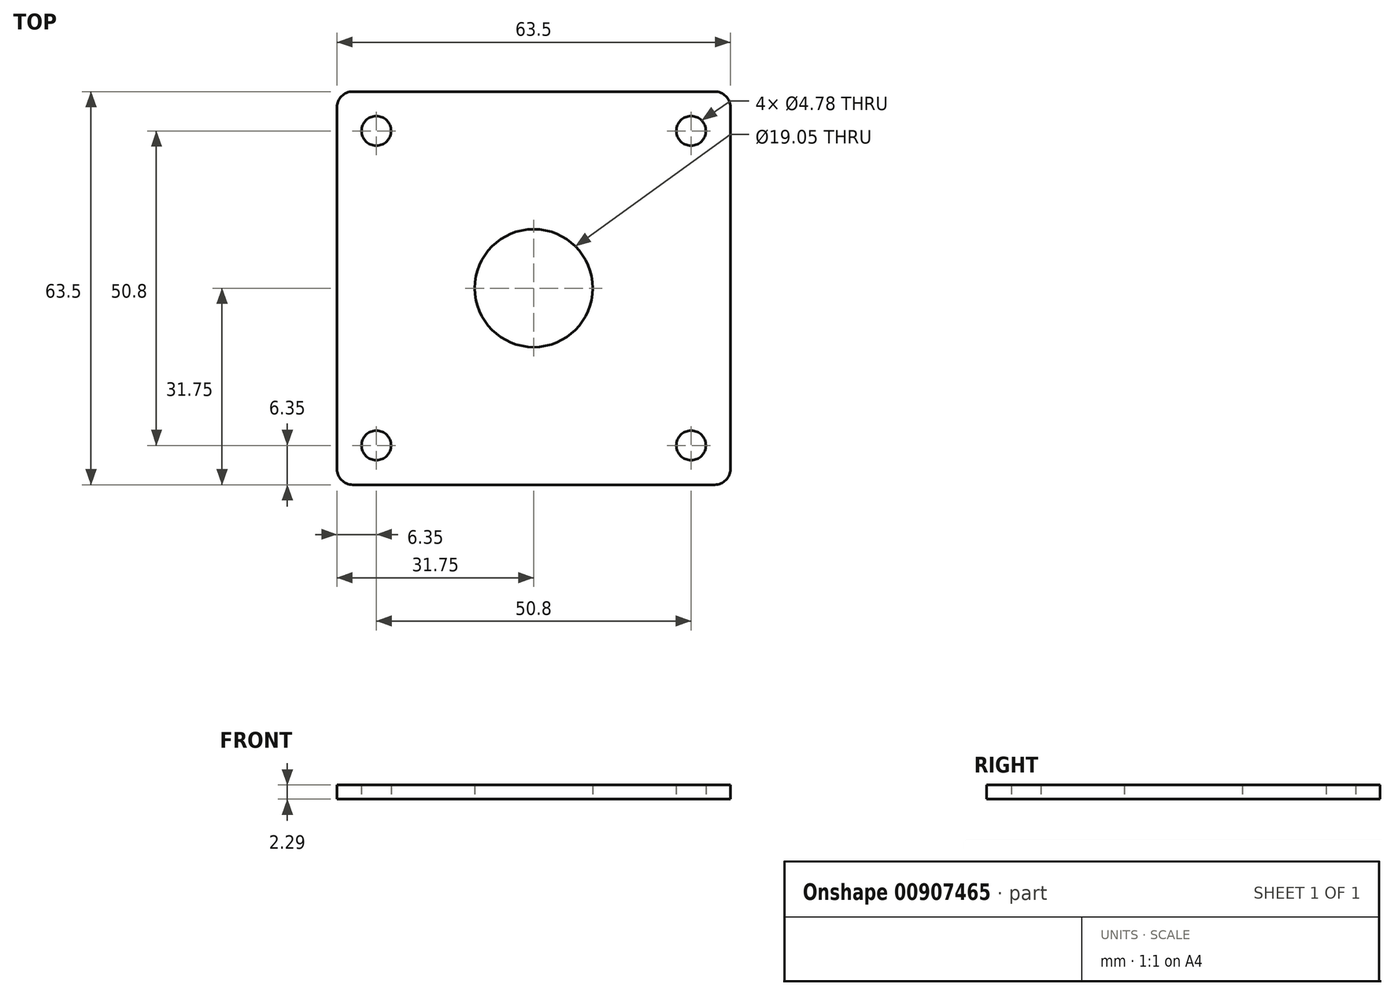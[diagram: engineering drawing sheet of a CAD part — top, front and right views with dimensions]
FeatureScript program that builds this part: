
annotation { "Feature Type Name" : "Feature", "Feature Type Description" : "" }
export const myFeature = defineFeature(function(context is Context, id is Id, definition is map)
    precondition{}
    {
        {
            var Q0;
            Q0=qCreatedBy(makeId("Top.planeOp"),FACE);
            var sketch = newSketch(context, id + "F0", { "sketchPlane" : qUnion([Q0])});
            skLineSegment(sketch, "E0.bottom", {"start": v(29.21, -31.75) * mm, "end": v(-29.21, -31.75) * mm});
            skLineSegment(sketch, "E0.top", {"start": v(29.21, 31.75) * mm, "end": v(-29.2, 31.75) * mm});
            skLineSegment(sketch, "E0.left", {"start": v(31.75, -29.2) * mm, "end": v(31.75, 29.21) * mm});
            skLineSegment(sketch, "E0.right", {"start": v(-31.75, -29.21) * mm, "end": v(-31.75, 29.2) * mm});
            skPoint(sketch, "E0.middle", {"position": v(0, 0) * mm});
            skCircle(sketch, "E1", {"center": v(0, 0) * mm, "radius": 9.53 * mm});
            skCircle(sketch, "E2", {"center": v(25.4, 25.4) * mm, "radius": 2.39 * mm});
            skLineSegment(sketch, "E3", {"start": v(0, -40.94) * mm, "end": v(0, 46.29) * mm, "construction": true});
            skLineSegment(sketch, "E4", {"start": v(-47.18, 0) * mm, "end": v(40.45, 0) * mm, "construction": true});
            skCircle(sketch, "E5.MirrorC", {"center": v(-25.4, 25.4) * mm, "radius": 2.39 * mm});
            skCircle(sketch, "E6.MirrorC", {"center": v(25.4, -25.4) * mm, "radius": 2.39 * mm});
            skCircle(sketch, "E7.MirrorC", {"center": v(-25.4, -25.4) * mm, "radius": 2.39 * mm});
            skPoint(sketch, "E8.visualSharp", {"position": v(-31.75, 31.75) * mm});
            skArc(sketch, "E8.filletArc", {"start": v(-29.2, 31.75) * mm, "mid": v(-31, 31) * mm, "end": v(-31.75, 29.2) * mm});
            skPoint(sketch, "E9.visualSharp", {"position": v(-31.75, -31.75) * mm});
            skArc(sketch, "E9.filletArc", {"start": v(-31.75, -29.21) * mm, "mid": v(-31, -31) * mm, "end": v(-29.21, -31.75) * mm});
            skPoint(sketch, "E10.visualSharp", {"position": v(31.75, -31.75) * mm});
            skArc(sketch, "E10.filletArc", {"start": v(29.21, -31.75) * mm, "mid": v(31, -31) * mm, "end": v(31.75, -29.2) * mm});
            skPoint(sketch, "E11.visualSharp", {"position": v(31.75, 31.75) * mm});
            skArc(sketch, "E11.filletArc", {"start": v(31.75, 29.21) * mm, "mid": v(31, 31) * mm, "end": v(29.21, 31.75) * mm});
            skSolve(sketch);
        }
        {
            var Q0;
            Q0=qSketchRegion(id+"F0",true);
            extrude(context, id + "F1", {"entities" : qUnion([Q0]), "depth" : 2.3 * mm, "offsetDistance" : 25.4 * mm});
        }
    });
